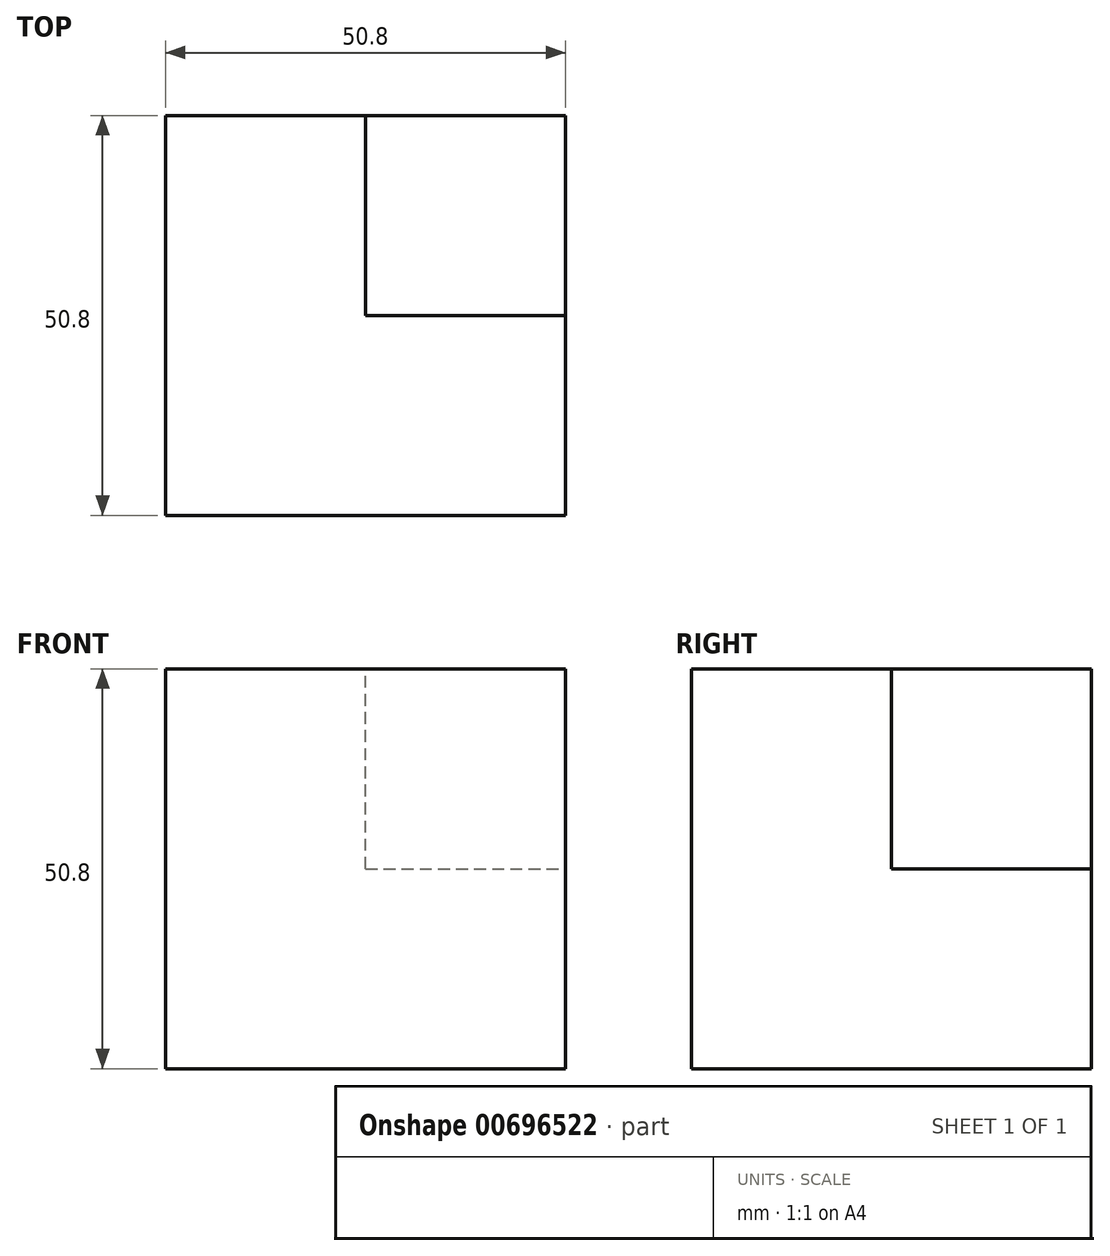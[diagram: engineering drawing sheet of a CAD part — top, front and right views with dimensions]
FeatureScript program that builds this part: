
annotation { "Feature Type Name" : "Feature", "Feature Type Description" : "" }
export const myFeature = defineFeature(function(context is Context, id is Id, definition is map)
    precondition{}
    {
        {
            var Q0;
            Q0=qCreatedBy(makeId("Right.planeOp"),FACE);
            var sketch = newSketch(context, id + "F0", { "sketchPlane" : qUnion([Q0])});
            skLineSegment(sketch, "E0.bottom", {"start": v(0, 0) * mm, "end": v(50.8, 0) * mm});
            skLineSegment(sketch, "E0.top", {"start": v(0, 50.8) * mm, "end": v(50.8, 50.8) * mm});
            skLineSegment(sketch, "E0.left", {"start": v(0, 0) * mm, "end": v(0, 50.8) * mm});
            skLineSegment(sketch, "E0.right", {"start": v(50.8, 0) * mm, "end": v(50.8, 50.8) * mm});
            skSolve(sketch);
        }
        {
            var Q0;
            Q0=makeQuery(id+"F0.imprint","IMPRINT",FACE,{"disambiguationData":[TD([[makeQuery(id+"F0.imprint","IMPRINT",EDGE,{"derivedFrom":sQuery(id+"F0.wireOp",EDGE,"E0.bottom")}),1.0]])]});
            extrude(context, id + "F1", {"entities" : qUnion([Q0]), "depth" : 50.8 * mm, "offsetDistance" : 25.4 * mm});
        }
        {
            var Q0;
            Q0=makeQuery(id+"F1.opExtrude","CAP_FACE",FACE,{"disambiguationData":[OSD([sQuery(id+"F0.wireOp",EDGE,"E0.bottom"),sQuery(id+"F0.wireOp",EDGE,"E0.top"),sQuery(id+"F0.wireOp",EDGE,"E0.left"),sQuery(id+"F0.wireOp",EDGE,"E0.right")])],"isStart":false});
            var sketch = newSketch(context, id + "F2", { "sketchPlane" : qUnion([Q0])});
            skLineSegment(sketch, "E1.bottom", {"start": v(50.8, 50.8) * mm, "end": v(25.4, 50.8) * mm});
            skLineSegment(sketch, "E1.top", {"start": v(50.8, 25.4) * mm, "end": v(25.4, 25.4) * mm});
            skLineSegment(sketch, "E1.left", {"start": v(50.8, 50.8) * mm, "end": v(50.8, 25.4) * mm});
            skLineSegment(sketch, "E1.right", {"start": v(25.4, 50.8) * mm, "end": v(25.4, 25.4) * mm});
            skSolve(sketch);
        }
        {
            var Q0;
            Q0=makeQuery(id+"F2.imprint","IMPRINT",FACE,{"disambiguationData":[TD([[makeQuery(id+"F2.imprint","IMPRINT",EDGE,{"derivedFrom":sQuery(id+"F2.wireOp",EDGE,"E1.bottom")}),-1.0]])]});
            extrude(context, id + "F3", {"entities" : qUnion([Q0]), "operationType" : NewBodyOperationType.REMOVE, "oppositeDirection" : true, "depth" : 25.4 * mm, "offsetDistance" : 25.4 * mm});
        }
    });
